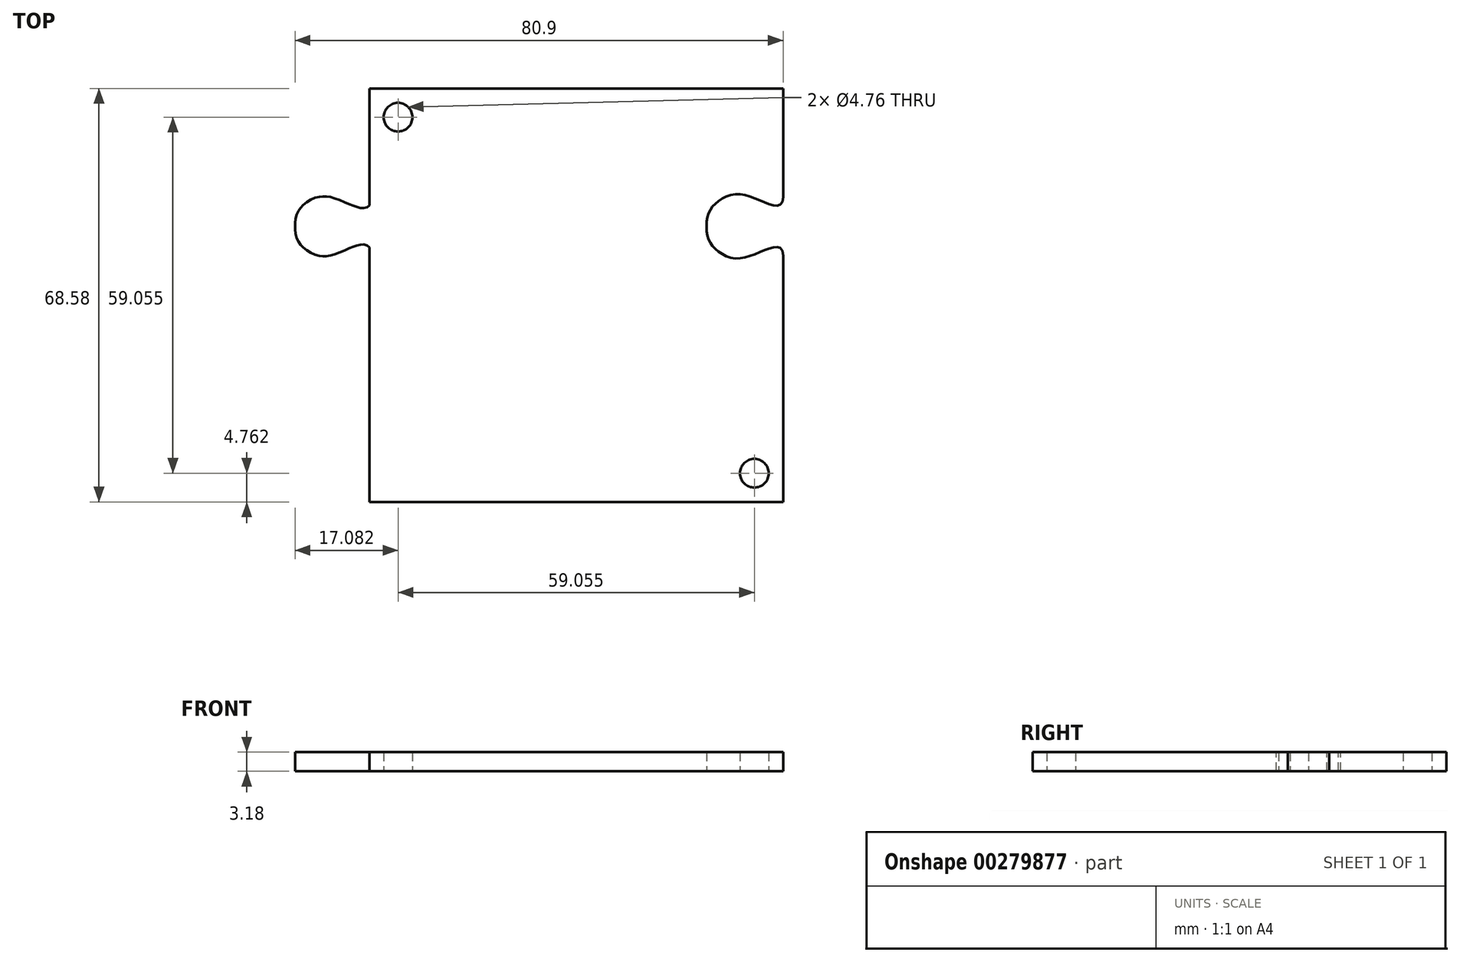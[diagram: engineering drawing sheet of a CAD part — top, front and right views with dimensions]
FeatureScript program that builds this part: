
annotation { "Feature Type Name" : "Feature", "Feature Type Description" : "" }
export const myFeature = defineFeature(function(context is Context, id is Id, definition is map)
    precondition{}
    {
        {
            var Q0;
            Q0=qCreatedBy(makeId("Top.planeOp"),FACE);
            var sketch = newSketch(context, id + "F0", { "sketchPlane" : qUnion([Q0])});
            skLineSegment(sketch, "E0.bottom", {"start": v(34.3, 34.3) * mm, "end": v(-34.3, 34.3) * mm});
            skLineSegment(sketch, "E0.top", {"start": v(34.3, -34.3) * mm, "end": v(-34.3, -34.3) * mm});
            skLineSegment(sketch, "E0.left", {"start": v(34.3, 34.3) * mm, "end": v(34.3, -34.3) * mm});
            skLineSegment(sketch, "E0.right", {"start": v(-34.3, 34.3) * mm, "end": v(-34.3, -34.3) * mm});
            skPoint(sketch, "E0.middle", {"position": v(0, 0) * mm});
            skCircle(sketch, "E1", {"center": v(-29.53, 29.53) * mm, "radius": 2.38 * mm});
            skCircle(sketch, "E2.MirrorC", {"center": v(29.53, -29.53) * mm, "radius": 2.38 * mm});
            skSolve(sketch);
        }
        {
            var Q0;
            Q0 = qSketchRegion(id + "F0", true);
            extrude(context, id + "F1", {"entities" : qUnion([Q0]), "depth" : 3.17 * mm});
        }
        {
            var Q0;
            Q0=qCreatedBy(makeId("Top.planeOp"),FACE);
            var sketch = newSketch(context, id + "F2", { "sketchPlane" : qUnion([Q0])});
            skPoint(sketch, "E3", {"position": v(-34.3, 16.33) * mm});
            skPoint(sketch, "E4", {"position": v(-36.2, 14.99) * mm});
            skPoint(sketch, "E5", {"position": v(-41.66, 16.76) * mm});
            skPoint(sketch, "E6", {"position": v(-45.72, 14.99) * mm});
            skPoint(sketch, "E7", {"position": v(-47, 11.43) * mm});
            skFitSpline(sketch, "E8", {"points": [v(-34.3, 16.33) * mm, v(-36.2, 14.99) * mm, v(-41.66, 16.76) * mm, v(-45.72, 14.99) * mm, v(-47, 11.43) * mm], "startDerivative": vector(0, -24.54) * mm, "endDerivative": vector(0, -20.15) * mm});
            skLineSegment(sketch, "E9", {"start": v(-47, 11.43) * mm, "end": v(-29.95, 11.43) * mm, "construction": true});
            skFitSpline(sketch, "E10.MirrorCS", {"points": [v(-34.3, 6.53) * mm, v(-36.2, 7.87) * mm, v(-41.66, 6.1) * mm, v(-45.72, 7.87) * mm, v(-47, 11.43) * mm], "startDerivative": vector(0, 24.54) * mm, "endDerivative": vector(0, 20.15) * mm});
            skLineSegment(sketch, "E11", {"start": v(-34.3, 16.33) * mm, "end": v(-34.3, 6.53) * mm, "construction": true});
            skFitSpline(sketch, "E12.MirrorCS", {"points": [v(-34.3, 16.33) * mm, v(-32.39, 14.99) * mm, v(-26.92, 16.76) * mm, v(-22.86, 14.99) * mm, v(-21.59, 11.43) * mm], "startDerivative": vector(0, -24.54) * mm, "endDerivative": vector(0, -20.15) * mm});
            skFitSpline(sketch, "E13.MirrorCS", {"points": [v(-34.3, 6.53) * mm, v(-32.39, 7.87) * mm, v(-26.92, 6.1) * mm, v(-22.86, 7.87) * mm, v(-21.59, 11.43) * mm], "startDerivative": vector(0, 24.54) * mm, "endDerivative": vector(0, 20.15) * mm});
            skFitSpline(sketch, "E14.0", {"points": [v(-33.9, 6.53) * mm, v(-33.9, 6.8) * mm, v(-33.96, 7.3) * mm, v(-34.16, 7.77) * mm, v(-34.42, 8.07) * mm, v(-34.73, 8.28) * mm, v(-35.16, 8.4) * mm, v(-35.7, 8.38) * mm, v(-36.22, 8.27) * mm, v(-36.76, 8.1) * mm, v(-37.5, 7.83) * mm, v(-38.44, 7.42) * mm, v(-39.6, 6.94) * mm, v(-40.54, 6.64) * mm, v(-41.28, 6.5) * mm, v(-41.8, 6.46) * mm, v(-42.32, 6.5) * mm, v(-43, 6.62) * mm, v(-43.8, 6.91) * mm, v(-44.68, 7.44) * mm, v(-45.29, 7.96) * mm, v(-45.69, 8.4) * mm, v(-46.02, 8.85) * mm, v(-46.33, 9.45) * mm, v(-46.56, 10.3) * mm, v(-46.6, 11.03) * mm, v(-46.6, 11.43) * mm]});
            skFitSpline(sketch, "E14.1", {"points": [v(-33.9, 16.33) * mm, v(-33.9, 16.05) * mm, v(-33.96, 15.56) * mm, v(-34.16, 15.09) * mm, v(-34.42, 14.8) * mm, v(-34.73, 14.58) * mm, v(-35.16, 14.46) * mm, v(-35.7, 14.48) * mm, v(-36.22, 14.6) * mm, v(-36.76, 14.76) * mm, v(-37.5, 15.03) * mm, v(-38.44, 15.44) * mm, v(-39.6, 15.92) * mm, v(-40.54, 16.22) * mm, v(-41.28, 16.36) * mm, v(-41.8, 16.4) * mm, v(-42.32, 16.37) * mm, v(-43, 16.24) * mm, v(-43.8, 15.95) * mm, v(-44.68, 15.42) * mm, v(-45.29, 14.9) * mm, v(-45.69, 14.46) * mm, v(-46.02, 14.01) * mm, v(-46.33, 13.41) * mm, v(-46.56, 12.55) * mm, v(-46.6, 11.83) * mm, v(-46.6, 11.43) * mm]});
            skLineSegment(sketch, "E15", {"start": v(-34.3, 16.33) * mm, "end": v(-34.3, 6.53) * mm});
            skLineSegment(sketch, "E16", {"start": v(-34.3, 7.92) * mm, "end": v(-34.3, 14.94) * mm});
            skFitSpline(sketch, "E17.MirrorCS", {"points": [v(34.3, 16.33) * mm, v(32.39, 14.99) * mm, v(26.92, 16.76) * mm, v(22.86, 14.99) * mm, v(21.59, 11.43) * mm], "startDerivative": vector(0, -24.54) * mm, "endDerivative": vector(0, -20.15) * mm});
            skFitSpline(sketch, "E18.MirrorCS", {"points": [v(34.3, 6.53) * mm, v(32.39, 7.87) * mm, v(26.92, 6.1) * mm, v(22.86, 7.87) * mm, v(21.59, 11.43) * mm], "startDerivative": vector(0, 24.54) * mm, "endDerivative": vector(0, 20.15) * mm});
            skLineSegment(sketch, "E19", {"start": v(34.3, 16.33) * mm, "end": v(39.12, 16.33) * mm});
            skLineSegment(sketch, "E20", {"start": v(39.12, 16.33) * mm, "end": v(39.12, 6.53) * mm});
            skLineSegment(sketch, "E21", {"start": v(39.12, 6.53) * mm, "end": v(34.3, 6.53) * mm});
            skSolve(sketch);
        }
        {
            var Q0;
            Q0=makeQuery(id+"F2.imprint","IMPRINT",FACE,{"disambiguationData":[TD([[makeQuery(id+"F2.imprint","IMPRINT",EDGE,{"derivedFrom":sQuery(id+"F2.wireOp",EDGE,"E14.0")}),-1.0]])]});
            var Q1;
            Q1=makeQuery(id+"F1.opExtrude","CAP_FACE",FACE,{"disambiguationData":[OSD([sQuery(id+"F0.wireOp",EDGE,"E0.bottom"),sQuery(id+"F0.wireOp",EDGE,"E0.top"),sQuery(id+"F0.wireOp",EDGE,"E0.left"),sQuery(id+"F0.wireOp",EDGE,"E0.right"),sQuery(id+"F0.wireOp",EDGE,"E1"),sQuery(id+"F0.wireOp",EDGE,"e1648c08-8adf-473f-9b64-c467cf328ef90.MirrorC"),sQuery(id+"F0.wireOp",EDGE,"1cdcda55-2210-49d8-b5f0-9198a802923b0.MirrorC"),sQuery(id+"F0.wireOp",EDGE,"E2.MirrorC")])],"isStart":false});
            extrude(context, id + "F3", {"entities" : qUnion([Q0]), "operationType" : NewBodyOperationType.ADD, "endBound" : BoundingType.UP_TO_SURFACE, "endBoundEntityFace" : qUnion([Q1]), "depth" : 25.4 * mm});
        }
        {
            var Q0;
            Q0=qCreatedBy(makeId("Right.planeOp"),FACE);
            var sketch = newSketch(context, id + "F4", { "sketchPlane" : qUnion([Q0])});
            skLineSegment(sketch, "E22", {"start": v(0, -65.87) * mm, "end": v(0, 47.63) * mm});
            skSolve(sketch);
        }
        {
            var Q0;
            Q0=makeQuery(id+"F2.imprint","IMPRINT",FACE,{"disambiguationData":[TD([[makeQuery(id+"F2.imprint","IMPRINT",EDGE,{"derivedFrom":sQuery(id+"F2.wireOp",EDGE,"E17.MirrorCS")}),1.0]])]});
            extrude(context, id + "F5", {"entities" : qUnion([Q0]), "operationType" : NewBodyOperationType.REMOVE, "endBound" : BoundingType.THROUGH_ALL, "depth" : 25.4 * mm});
        }
    });
